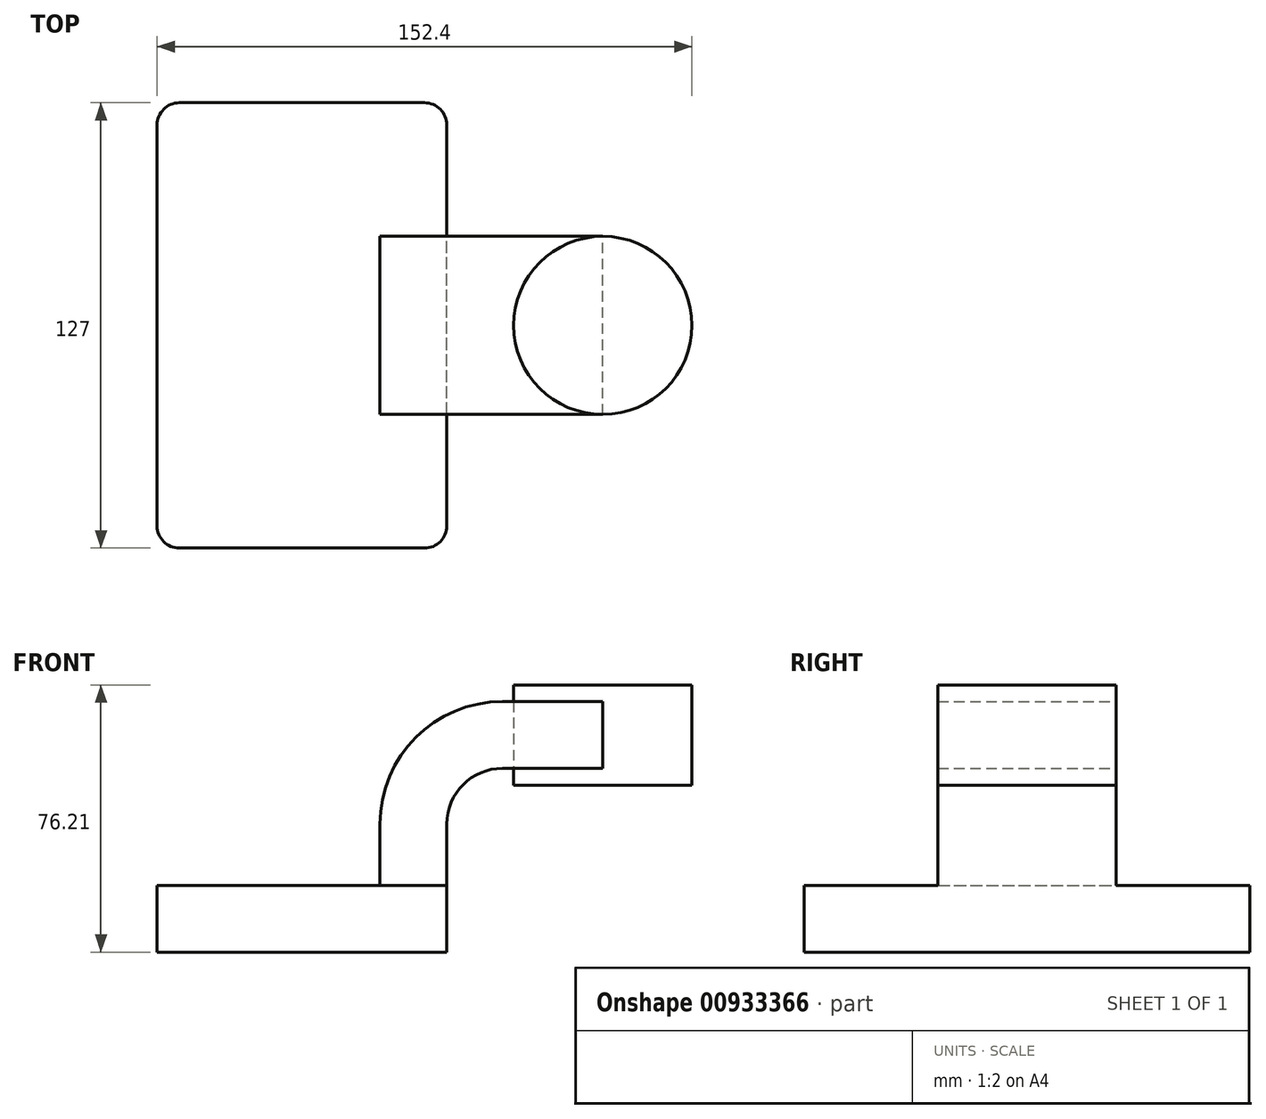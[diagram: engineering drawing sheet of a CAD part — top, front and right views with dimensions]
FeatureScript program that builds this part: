
annotation { "Feature Type Name" : "Feature", "Feature Type Description" : "" }
export const myFeature = defineFeature(function(context is Context, id is Id, definition is map)
    precondition{}
    {
        {
            var Q0;
            Q0=qCreatedBy(makeId("Front.planeOp"),FACE);
            var sketch = newSketch(context, id + "F0", { "sketchPlane" : qUnion([Q0])});
            skLineSegment(sketch, "E0.bottom", {"start": v(-41.28, 9.52) * mm, "end": v(41.27, 9.53) * mm});
            skLineSegment(sketch, "E0.top", {"start": v(-41.28, -9.53) * mm, "end": v(41.28, -9.53) * mm});
            skLineSegment(sketch, "E0.left", {"start": v(-41.28, 9.52) * mm, "end": v(-41.27, -9.53) * mm});
            skLineSegment(sketch, "E0.right", {"start": v(41.28, 9.53) * mm, "end": v(41.28, -9.52) * mm});
            skPoint(sketch, "E0.middle", {"position": v(0, 0) * mm});
            skLineSegment(sketch, "E1.bottom", {"start": v(60.32, 38.1) * mm, "end": v(111.12, 38.1) * mm});
            skLineSegment(sketch, "E1.top", {"start": v(60.32, 66.67) * mm, "end": v(111.12, 66.67) * mm});
            skLineSegment(sketch, "E1.left", {"start": v(60.32, 38.1) * mm, "end": v(60.32, 66.67) * mm});
            skLineSegment(sketch, "E1.right", {"start": v(111.12, 38.1) * mm, "end": v(111.12, 66.67) * mm});
            skPoint(sketch, "E1.middle", {"position": v(85.72, 52.39) * mm});
            skLineSegment(sketch, "E2", {"start": v(41.27, 9.53) * mm, "end": v(41.27, 27) * mm});
            skArc(sketch, "E3", {"start": v(41.27, 27) * mm, "mid": v(45.92, 38.23) * mm, "end": v(57.15, 42.88) * mm});
            skLineSegment(sketch, "E4", {"start": v(57.15, 42.88) * mm, "end": v(85.72, 42.88) * mm});
            skLineSegment(sketch, "E5.0", {"start": v(57.15, 61.93) * mm, "end": v(85.72, 61.93) * mm});
            skArc(sketch, "E5.1", {"start": v(22.22, 27) * mm, "mid": v(32.45, 51.7) * mm, "end": v(57.15, 61.93) * mm});
            skLineSegment(sketch, "E5.2", {"start": v(22.22, 9.53) * mm, "end": v(22.22, 27) * mm});
            skLineSegment(sketch, "E6", {"start": v(85.72, 38.1) * mm, "end": v(85.72, 66.67) * mm});
            skFitSpline(sketch, "E7", {"points": [v(-41.28, 9.52) * mm, v(57.15, 61.93) * mm], "startDerivative": vector(69.42, 96.93) * mm, "endDerivative": vector(129.04, -29.69) * mm});
            skSolve(sketch);
        }
        {
            var Q0;
            Q0=makeQuery(id+"F0.imprint","IMPRINT",FACE,{"disambiguationData":[TD([[makeQuery(id+"F0.imprint","IMPRINT",EDGE,{"derivedFrom":sQuery(id+"F0.wireOp",EDGE,"E0.top")}),1.0]])]});
            extrude(context, id + "F1", {"entities" : qUnion([Q0]), "endBound" : BoundingType.SYMMETRIC, "depth" : 127 * mm, "offsetDistance" : 25.4 * mm});
        }
        {
            var Q0;
            {var subQ1=sQuery(id+"F0.wireOp",EDGE,"E2");Q0=makeQuery(id+"F0.imprint","IMPRINT",FACE,{"disambiguationData":[TD([[makeQuery(id+"F0.imprint","IMPRINT",EDGE,{"derivedFrom":subQ1}),1.0]])]});}
            var Q1;
            {var subQ0=sQuery(id+"F0.wireOp",EDGE,"E4");var subQ1=sQuery(id+"F0.wireOp",EDGE,"E1.left");var subQ2=makeQuery(id+"F0.imprint","INTERSECT",VERTEX,{"derivedFrom":[subQ1,subQ0]});Q1=makeQuery(id+"F0.imprint","IMPRINT",FACE,{"disambiguationData":[TD([[makeQuery(id+"F0.imprint","IMPRINT",EDGE,{"disambiguationData":[TD([[subQ2,-1.0]])],"derivedFrom":subQ1}),-1.0]])]});}
            extrude(context, id + "F2", {"entities" : qUnion([Q0, Q1]), "operationType" : NewBodyOperationType.ADD, "endBound" : BoundingType.SYMMETRIC, "depth" : 50.8 * mm, "offsetDistance" : 25.4 * mm});
        }
        {
            var Q0;
            Q0=makeQuery(id+"F0.imprint","IMPRINT",FACE,{"disambiguationData":[TD([[makeQuery(id+"F0.imprint","IMPRINT",EDGE,{"derivedFrom":sQuery(id+"F0.wireOp",EDGE,"E5.1")}),1.0]])]});
            extrude(context, id + "F3", {"entities" : qUnion([Q0]), "operationType" : NewBodyOperationType.ADD, "depth" : 15.88 * mm, "offsetDistance" : 25.4 * mm});
        }
        {
            var Q0;
            {var subQ0=sQuery(id+"F0.wireOp",EDGE,"E1.right");Q0=makeQuery(id+"F0.imprint","IMPRINT",FACE,{"disambiguationData":[TD([[makeQuery(id+"F0.imprint","IMPRINT",EDGE,{"derivedFrom":subQ0}),1.0]])]});}
            var Q1;
            Q1=sQuery(id+"F0.wireOp",EDGE,"E6");
            revolve(context, id + "F4", {"surfaceOperationType" : NewSurfaceOperationType.NEW, "entities" : qUnion([Q0]), "axis" : qUnion([Q1]), "revolveType" : RevolveType.FULL});
        }
        {
            var Q0;
            Q0=makeQuery(id+"F1.opExtrude","CAP_EDGE",EDGE,{"disambiguationData":[OSD([sQuery(id+"F0.wireOp",EDGE,"E0.left")])],"isStart":false});
            var Q1;
            Q1=makeQuery(id+"F1.opExtrude","CAP_EDGE",EDGE,{"disambiguationData":[OSD([sQuery(id+"F0.wireOp",EDGE,"E0.right")])],"isStart":false});
            var Q2;
            Q2=makeQuery(id+"F1.opExtrude","CAP_EDGE",EDGE,{"disambiguationData":[OSD([sQuery(id+"F0.wireOp",EDGE,"E0.left")])],"isStart":true});
            var Q3;
            Q3=makeQuery(id+"F1.opExtrude","CAP_EDGE",EDGE,{"disambiguationData":[OSD([sQuery(id+"F0.wireOp",EDGE,"E0.right")])],"isStart":true});
            fillet(context, id + "F5", {"entities" : qUnion([Q0, Q1, Q2, Q3]), "radius" : 6.35 * mm, "tangentPropagation" : true, "allowEdgeOverflow" : false});
        }
    });
